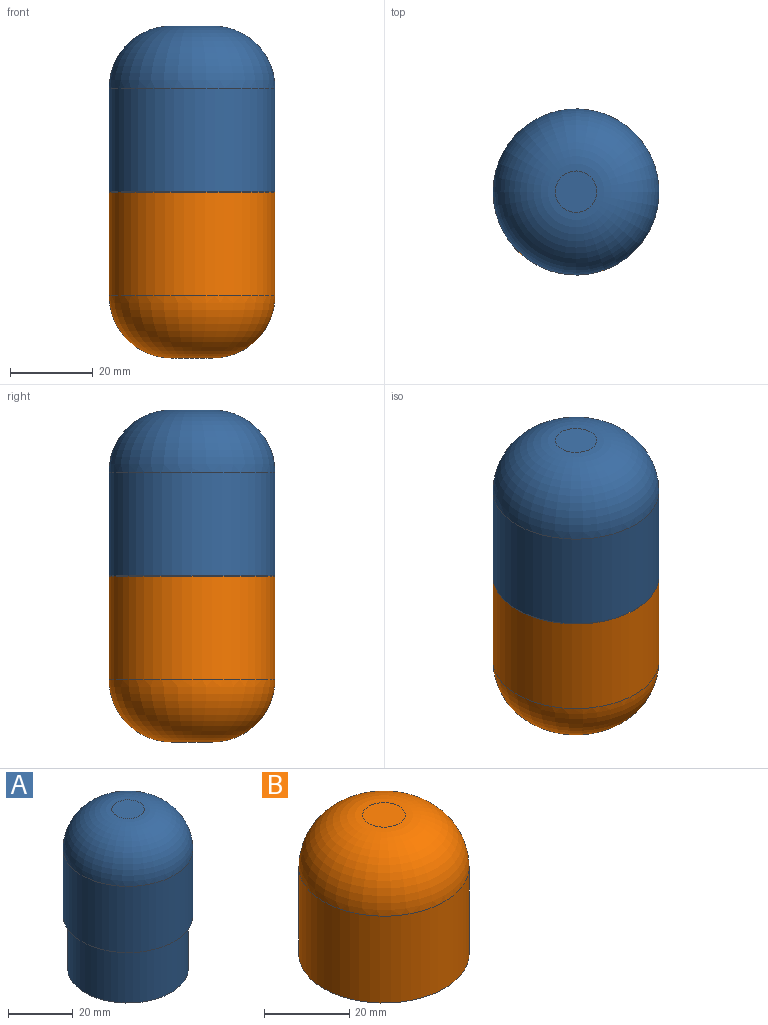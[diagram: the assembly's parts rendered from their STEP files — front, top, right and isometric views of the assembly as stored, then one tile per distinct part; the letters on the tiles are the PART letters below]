
ASSEMBLY  parts=2 mates=1
PART A: 11 faces, bbox 40x40x60 mm
  f0: cylinder r=20mm len=40mm, axis (0,0,-1), area 3141.6mm2, adj f1,f5
  f1: plane 40x40mm, normal (0,0,-1), area 169.8mm2, adj f0,f2
  f2: cylinder r=18.6mm len=37.2mm, axis (0,0,-1), area 2337.3mm2, adj f1,f3
  f3: plane 37.2x37.2mm, normal (0,0,-1), area 113.7mm2, adj f2,f8
  f4: plane 10x10mm, normal (0,0,1), area 78.5mm2, adj f5
  f5: torus R=5mm, axis (0,0,-1), area 2153.9mm2, adj f0,f4
  f6: cylinder r=19mm len=38mm, axis (0,0,-1), area 2865.1mm2, adj f7,f10
  f7: plane 38x38mm, normal (0,0,1), area 161mm2, adj f6,f8
  f8: cylinder r=17.6mm len=35.2mm, axis (0,0,-1), area 2322.3mm2, adj f3,f7
  f9: plane 10x10mm, normal (0,0,-1), area 78.5mm2, adj f10
  f10: torus R=5mm, axis (0,0,-1), area 1922.4mm2, adj f6,f9
PART B: 7 faces, bbox 40x40x40 mm
  f0: plane 40x40mm, normal (0,0,-1), area 122.5mm2, adj f3,f6
  f1: plane 10x10mm, normal (0,0,1), area 78.5mm2, adj f2
  f2: torus R=5mm, axis (0,0,-1), area 2153.9mm2, adj f1,f3
  f3: cylinder r=20mm len=40mm, axis (0,0,-1), area 3141.6mm2, adj f0,f2
  f4: plane 10x10mm, normal (0,0,-1), area 78.5mm2, adj f5
  f5: torus R=5mm, axis (0,0,-1), area 1922.4mm2, adj f4,f6
  f6: cylinder r=19mm len=38mm, axis (0,0,-1), area 2984.5mm2, adj f0,f5
PLACE A t=(75.58,2.83,-49.59)mm
PLACE B rot(axis=(1,0,0),180deg) t=(75.58,2.83,-29.65)mm
MATE slider B.f2 <-> A.f0  axis (0,0,1) through (75.58,2.83,-29.65)mm
